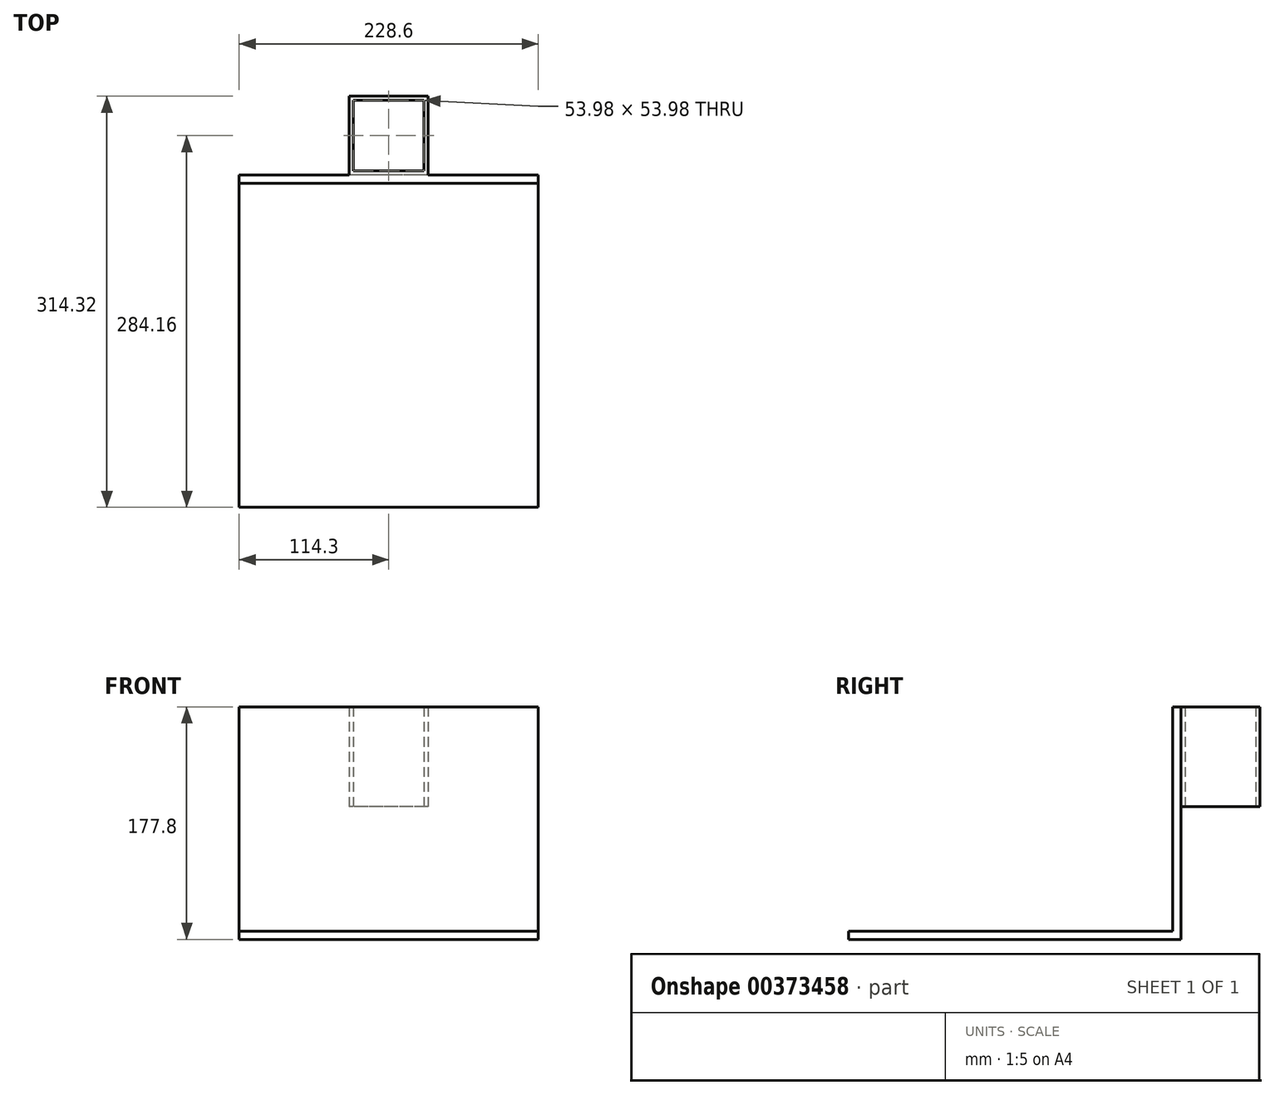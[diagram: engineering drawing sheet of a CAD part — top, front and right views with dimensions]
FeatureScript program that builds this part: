
annotation { "Feature Type Name" : "Feature", "Feature Type Description" : "" }
export const myFeature = defineFeature(function(context is Context, id is Id, definition is map)
    precondition{}
    {
        {
            var Q0;
            Q0=qCreatedBy(makeId("Top.planeOp"),FACE);
            var sketch = newSketch(context, id + "F0", { "sketchPlane" : qUnion([Q0])});
            skLineSegment(sketch, "E0.bottom", {"start": v(26.99, -26.99) * mm, "end": v(-26.99, -26.99) * mm});
            skLineSegment(sketch, "E0.top", {"start": v(26.99, 26.99) * mm, "end": v(-26.99, 26.99) * mm});
            skLineSegment(sketch, "E0.left", {"start": v(26.99, -26.99) * mm, "end": v(26.99, 26.99) * mm});
            skLineSegment(sketch, "E0.right", {"start": v(-26.99, -26.99) * mm, "end": v(-26.99, 26.99) * mm});
            skPoint(sketch, "E0.middle", {"position": v(0, 0) * mm});
            skLineSegment(sketch, "E1.0", {"start": v(-30.16, -30.16) * mm, "end": v(-30.16, 30.16) * mm});
            skLineSegment(sketch, "E1.1", {"start": v(30.16, -30.16) * mm, "end": v(-30.16, -30.16) * mm});
            skLineSegment(sketch, "E1.2", {"start": v(30.16, -30.16) * mm, "end": v(30.16, 30.16) * mm});
            skLineSegment(sketch, "E1.3", {"start": v(30.16, 30.16) * mm, "end": v(-30.16, 30.16) * mm});
            skSolve(sketch);
        }
        {
            var Q0;
            Q0=makeQuery(id+"F0.imprint","IMPRINT",FACE,{"disambiguationData":[TD([[makeQuery(id+"F0.imprint","IMPRINT",EDGE,{"derivedFrom":sQuery(id+"F0.wireOp",EDGE,"E0.bottom")}),1.0]])]});
            extrude(context, id + "F1", {"entities" : qUnion([Q0]), "depth" : 76.2 * mm});
        }
        {
            var Q0;
            Q0=qCreatedBy(makeId("Right.planeOp"),FACE);
            var sketch = newSketch(context, id + "F2", { "sketchPlane" : qUnion([Q0])});
            skLineSegment(sketch, "E2.bottom", {"start": v(-30.16, 76.2) * mm, "end": v(-36.51, 76.2) * mm});
            skLineSegment(sketch, "E2.top", {"start": v(-30.16, -101.6) * mm, "end": v(-284.16, -101.6) * mm});
            skLineSegment(sketch, "E2.left", {"start": v(-30.16, 76.2) * mm, "end": v(-30.16, -101.6) * mm});
            skLineSegment(sketch, "E2.right", {"start": v(-36.51, 76.2) * mm, "end": v(-36.51, -95.25) * mm});
            skLineSegment(sketch, "E3.right", {"start": v(-284.16, -101.6) * mm, "end": v(-284.16, -95.25) * mm});
            skLineSegment(sketch, "E4", {"start": v(-36.51, -95.25) * mm, "end": v(-284.16, -95.25) * mm});
            skSolve(sketch);
        }
        {
            var Q0;
            Q0 = qSketchRegion(id + "F2", true);
            extrude(context, id + "F3", {"entities" : qUnion([Q0]), "operationType" : NewBodyOperationType.ADD, "endBound" : BoundingType.SYMMETRIC, "depth" : 228.6 * mm});
        }
    });
